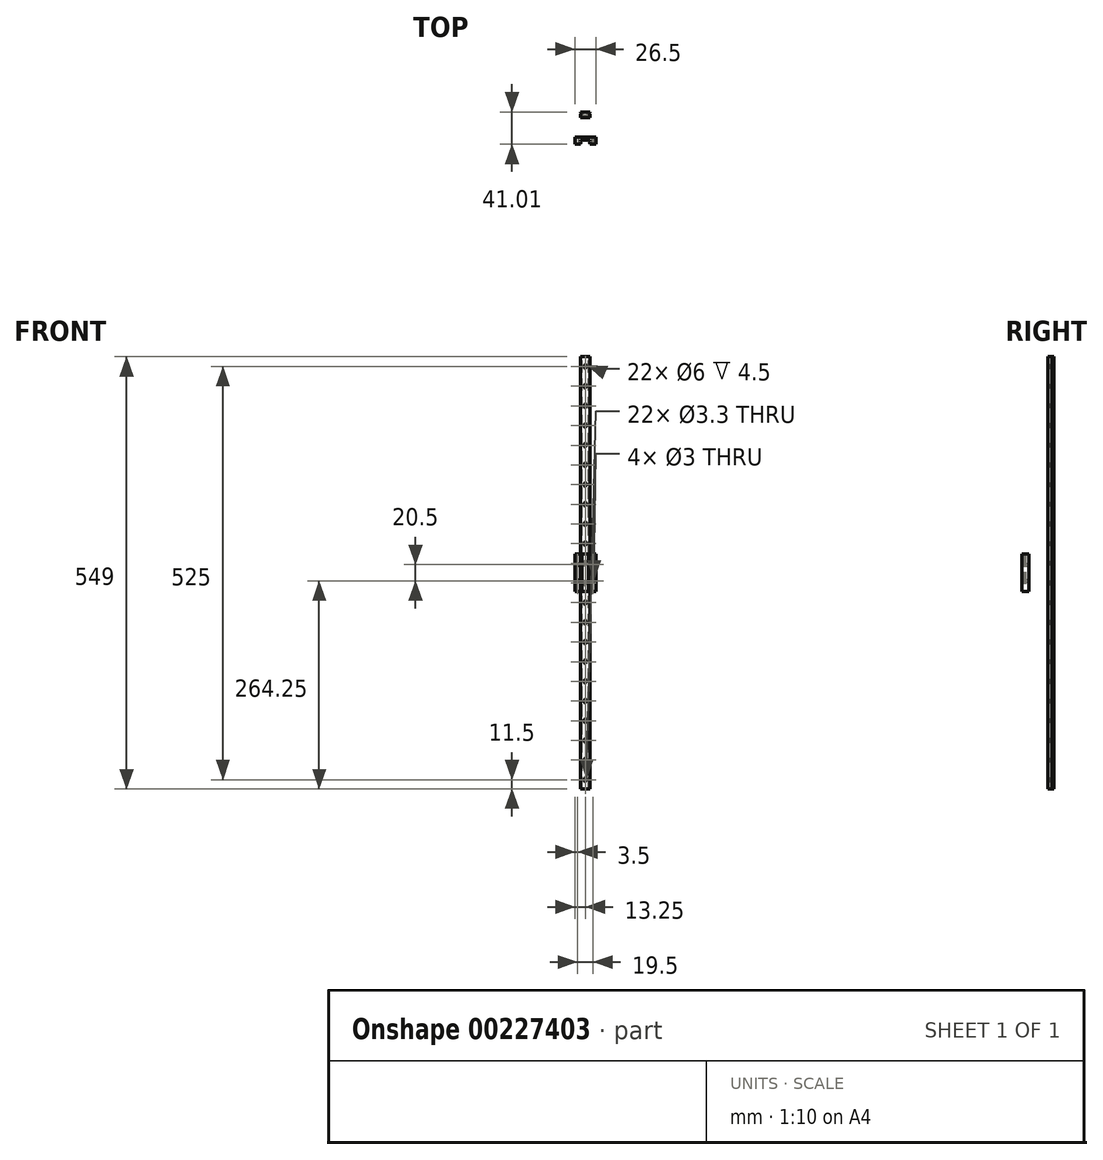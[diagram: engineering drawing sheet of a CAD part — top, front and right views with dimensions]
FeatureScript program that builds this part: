
annotation { "Feature Type Name" : "Feature", "Feature Type Description" : "" }
export const myFeature = defineFeature(function(context is Context, id is Id, definition is map)
    precondition{}
    {
        {
            var Q0;
            Q0=qCreatedBy(makeId("Front.planeOp"),FACE);
            var sketch = newSketch(context, id + "F0", { "sketchPlane" : qUnion([Q0])});
            skLineSegment(sketch, "E0.bottom", {"start": v(-6, 274.5) * mm, "end": v(6, 274.5) * mm});
            skLineSegment(sketch, "E0.top", {"start": v(-6, -274.5) * mm, "end": v(6, -274.5) * mm});
            skLineSegment(sketch, "E0.left", {"start": v(-6, 274.5) * mm, "end": v(-6, -274.5) * mm});
            skLineSegment(sketch, "E0.right", {"start": v(6, 274.5) * mm, "end": v(6, -274.5) * mm});
            skPoint(sketch, "E0.middle", {"position": v(0, 0) * mm});
            skSolve(sketch);
        }
        {
            var Q0;
            Q0 = qSketchRegion(id + "F0", true);
            extrude(context, id + "F1", {"entities" : qUnion([Q0]), "endBound" : BoundingType.SYMMETRIC, "depth" : 7.4 * mm});
        }
        {
            var Q0;
            Q0=makeQuery(id+"F1.opExtrude","SWEPT_FACE",FACE,{"disambiguationData":[OSD([sQuery(id+"F0.wireOp",EDGE,"E0.bottom")])]});
            var sketch = newSketch(context, id + "F2", { "sketchPlane" : qUnion([Q0])});
            skLineSegment(sketch, "E1", {"start": v(-6, 2.7) * mm, "end": v(-4, 1.7) * mm});
            skLineSegment(sketch, "E2", {"start": v(-4, 1.7) * mm, "end": v(-6, 1.03) * mm});
            skLineSegment(sketch, "E3.MirrorCS", {"start": v(6, 2.7) * mm, "end": v(4, 1.7) * mm});
            skLineSegment(sketch, "E4.MirrorCS", {"start": v(4, 1.7) * mm, "end": v(6, 1.03) * mm});
            skSolve(sketch);
        }
        {
            var Q0;
            {var subQ0=sQuery(id+"F2.wireOp",EDGE,"E1");Q0=makeQuery(id+"F2.imprint","IMPRINT",FACE,{"disambiguationData":[TD([[makeQuery(id+"F2.imprint","IMPRINT",EDGE,{"derivedFrom":subQ0}),-1.0]])]});}
            var Q1;
            {var subQ0=sQuery(id+"F2.wireOp",EDGE,"E3.MirrorCS");Q1=makeQuery(id+"F2.imprint","IMPRINT",FACE,{"disambiguationData":[TD([[makeQuery(id+"F2.imprint","IMPRINT",EDGE,{"derivedFrom":subQ0}),1.0]])]});}
            extrude(context, id + "F3", {"entities" : qUnion([Q0, Q1]), "operationType" : NewBodyOperationType.REMOVE, "endBound" : BoundingType.THROUGH_ALL, "oppositeDirection" : true, "depth" : 100 * mm});
        }
        {
            var Q0;
            Q0=makeQuery(id+"F1.opExtrude","CAP_FACE",FACE,{"disambiguationData":[OSD([sQuery(id+"F0.wireOp",EDGE,"E0.bottom"),sQuery(id+"F0.wireOp",EDGE,"E0.top"),sQuery(id+"F0.wireOp",EDGE,"E0.left"),sQuery(id+"F0.wireOp",EDGE,"E0.right")])],"isStart":true});
            var sketch = newSketch(context, id + "F4", { "sketchPlane" : qUnion([Q0])});
            skCircle(sketch, "E5", {"center": v(0, 262) * mm, "radius": 3 * mm});
            skPoint(sketch, "E6", {"position": v(0, 274.5) * mm});
            skCircle(sketch, "E7.0.1.0", {"center": v(0, 237) * mm, "radius": 3 * mm});
            skCircle(sketch, "E7.0.2.0", {"center": v(0, 212) * mm, "radius": 3 * mm});
            skCircle(sketch, "E7.0.3.0", {"center": v(0, 187) * mm, "radius": 3 * mm});
            skCircle(sketch, "E7.0.4.0", {"center": v(0, 162) * mm, "radius": 3 * mm});
            skCircle(sketch, "E7.0.5.0", {"center": v(0, 137) * mm, "radius": 3 * mm});
            skCircle(sketch, "E7.0.6.0", {"center": v(0, 112) * mm, "radius": 3 * mm});
            skCircle(sketch, "E7.0.7.0", {"center": v(0, 87) * mm, "radius": 3 * mm});
            skCircle(sketch, "E7.0.8.0", {"center": v(0, 62) * mm, "radius": 3 * mm});
            skCircle(sketch, "E7.0.9.0", {"center": v(0, 37) * mm, "radius": 3 * mm});
            skCircle(sketch, "E7.0.10.0", {"center": v(0, 12) * mm, "radius": 3 * mm});
            skCircle(sketch, "E7.0.11.0", {"center": v(0, -13) * mm, "radius": 3 * mm});
            skCircle(sketch, "E7.0.12.0", {"center": v(0, -38) * mm, "radius": 3 * mm});
            skCircle(sketch, "E7.0.13.0", {"center": v(0, -63) * mm, "radius": 3 * mm});
            skCircle(sketch, "E7.0.14.0", {"center": v(0, -88) * mm, "radius": 3 * mm});
            skCircle(sketch, "E7.0.15.0", {"center": v(0, -113) * mm, "radius": 3 * mm});
            skCircle(sketch, "E7.0.16.0", {"center": v(0, -138) * mm, "radius": 3 * mm});
            skCircle(sketch, "E7.0.17.0", {"center": v(0, -163) * mm, "radius": 3 * mm});
            skCircle(sketch, "E7.0.18.0", {"center": v(0, -188) * mm, "radius": 3 * mm});
            skCircle(sketch, "E7.0.19.0", {"center": v(0, -213) * mm, "radius": 3 * mm});
            skCircle(sketch, "E7.0.20.0", {"center": v(0, -238) * mm, "radius": 3 * mm});
            skCircle(sketch, "E7.0.21.0", {"center": v(0, -263) * mm, "radius": 3 * mm});
            skLineSegment(sketch, "E7.direction1", {"start": v(0, 262) * mm, "end": v(25, 262) * mm, "construction": true});
            skLineSegment(sketch, "E7.direction2", {"start": v(0, 262) * mm, "end": v(0, 237) * mm, "construction": true});
            skSolve(sketch);
        }
        {
            var Q0;
            Q0 = qSketchRegion(id + "F4", true);
            extrude(context, id + "F5", {"entities" : qUnion([Q0]), "operationType" : NewBodyOperationType.REMOVE, "oppositeDirection" : true, "depth" : 4.5 * mm});
        }
        {
            var Q0;
            Q0=makeQuery(id+"F1.opExtrude","CAP_FACE",FACE,{"disambiguationData":[OSD([sQuery(id+"F0.wireOp",EDGE,"E0.bottom"),sQuery(id+"F0.wireOp",EDGE,"E0.top"),sQuery(id+"F0.wireOp",EDGE,"E0.left"),sQuery(id+"F0.wireOp",EDGE,"E0.right")])],"isStart":false});
            var sketch = newSketch(context, id + "F6", { "sketchPlane" : qUnion([Q0])});
            skCircle(sketch, "E8", {"center": v(0, 262) * mm, "radius": 1.65 * mm});
            skCircle(sketch, "E9.0.1.0", {"center": v(0, 237) * mm, "radius": 1.65 * mm});
            skCircle(sketch, "E9.0.2.0", {"center": v(0, 212) * mm, "radius": 1.65 * mm});
            skCircle(sketch, "E9.0.3.0", {"center": v(0, 187) * mm, "radius": 1.65 * mm});
            skCircle(sketch, "E9.0.4.0", {"center": v(0, 162) * mm, "radius": 1.65 * mm});
            skCircle(sketch, "E9.0.5.0", {"center": v(0, 137) * mm, "radius": 1.65 * mm});
            skCircle(sketch, "E9.0.6.0", {"center": v(0, 112) * mm, "radius": 1.65 * mm});
            skCircle(sketch, "E9.0.7.0", {"center": v(0, 87) * mm, "radius": 1.65 * mm});
            skCircle(sketch, "E9.0.8.0", {"center": v(0, 62) * mm, "radius": 1.65 * mm});
            skCircle(sketch, "E9.0.9.0", {"center": v(0, 37) * mm, "radius": 1.65 * mm});
            skCircle(sketch, "E9.0.10.0", {"center": v(0, 12) * mm, "radius": 1.65 * mm});
            skCircle(sketch, "E9.0.11.0", {"center": v(0, -13) * mm, "radius": 1.65 * mm});
            skCircle(sketch, "E9.0.12.0", {"center": v(0, -38) * mm, "radius": 1.65 * mm});
            skCircle(sketch, "E9.0.13.0", {"center": v(0, -63) * mm, "radius": 1.65 * mm});
            skCircle(sketch, "E9.0.14.0", {"center": v(0, -88) * mm, "radius": 1.65 * mm});
            skCircle(sketch, "E9.0.15.0", {"center": v(0, -113) * mm, "radius": 1.65 * mm});
            skCircle(sketch, "E9.0.16.0", {"center": v(0, -138) * mm, "radius": 1.65 * mm});
            skCircle(sketch, "E9.0.17.0", {"center": v(0, -163) * mm, "radius": 1.65 * mm});
            skCircle(sketch, "E9.0.18.0", {"center": v(0, -188) * mm, "radius": 1.65 * mm});
            skCircle(sketch, "E9.0.19.0", {"center": v(0, -213) * mm, "radius": 1.65 * mm});
            skCircle(sketch, "E9.0.20.0", {"center": v(0, -238) * mm, "radius": 1.65 * mm});
            skCircle(sketch, "E9.0.21.0", {"center": v(0, -263) * mm, "radius": 1.65 * mm});
            skLineSegment(sketch, "E9.direction1", {"start": v(0, 262) * mm, "end": v(25, 262) * mm, "construction": true});
            skLineSegment(sketch, "E9.direction2", {"start": v(0, 262) * mm, "end": v(0, 237) * mm, "construction": true});
            skSolve(sketch);
        }
        {
            var Q0;
            Q0 = qSketchRegion(id + "F6", true);
            extrude(context, id + "F7", {"entities" : qUnion([Q0]), "operationType" : NewBodyOperationType.REMOVE, "oppositeDirection" : true, "depth" : 25 * mm});
        }
        {
            var Q0;
            Q0=qCreatedBy(makeId("Top.planeOp"),FACE);
            var sketch = newSketch(context, id + "F8", { "sketchPlane" : qUnion([Q0])});
            skLineSegment(sketch, "E10.bottom", {"start": v(-13.25, -28.3) * mm, "end": v(13.25, -28.3) * mm});
            skLineSegment(sketch, "E10.top", {"start": v(-13.25, -37.3) * mm, "end": v(-6, -37.3) * mm});
            skLineSegment(sketch, "E10.left", {"start": v(-13.25, -28.3) * mm, "end": v(-13.25, -37.3) * mm});
            skLineSegment(sketch, "E10.right", {"start": v(13.25, -28.3) * mm, "end": v(13.25, -37.3) * mm});
            skLineSegment(sketch, "E11.bottom", {"start": v(-6, -32.3) * mm, "end": v(6, -32.3) * mm});
            skLineSegment(sketch, "E12", {"start": v(-6, -33.3) * mm, "end": v(-4.16, -34.3) * mm});
            skLineSegment(sketch, "E13", {"start": v(-4.16, -34.3) * mm, "end": v(-6, -34.85) * mm});
            skLineSegment(sketch, "E14", {"start": v(-6, -32.3) * mm, "end": v(-6, -33.3) * mm});
            skLineSegment(sketch, "E15", {"start": v(-6, -34.85) * mm, "end": v(-6, -37.3) * mm});
            skLineSegment(sketch, "E16.MirrorCS", {"start": v(6, -33.3) * mm, "end": v(4.16, -34.3) * mm});
            skLineSegment(sketch, "E17.MirrorCS", {"start": v(4.16, -34.3) * mm, "end": v(6, -34.85) * mm});
            skLineSegment(sketch, "E18", {"start": v(6, -33.3) * mm, "end": v(6, -32.3) * mm});
            skLineSegment(sketch, "E19", {"start": v(6, -34.85) * mm, "end": v(6, -37.3) * mm});
            skLineSegment(sketch, "E20.trimOffspring", {"start": v(6, -37.3) * mm, "end": v(13.25, -37.3) * mm});
            skSolve(sketch);
        }
        {
            var Q0;
            Q0=makeQuery(id+"F8.imprint","IMPRINT",FACE,{"disambiguationData":[TD([[makeQuery(id+"F8.imprint","IMPRINT",EDGE,{"derivedFrom":sQuery(id+"F8.wireOp",EDGE,"E10.bottom")}),-1.0]])]});
            extrude(context, id + "F9", {"entities" : qUnion([Q0]), "endBound" : BoundingType.SYMMETRIC, "depth" : 47.5 * mm});
        }
        {
            var Q0;
            Q0=makeQuery(id+"F9.opExtrude","SWEPT_FACE",FACE,{"disambiguationData":[OSD([sQuery(id+"F8.wireOp",EDGE,"E10.bottom")])]});
            var sketch = newSketch(context, id + "F10", { "sketchPlane" : qUnion([Q0])});
            skCircle(sketch, "E21", {"center": v(9.75, -10.25) * mm, "radius": 1.5 * mm});
            skCircle(sketch, "E22.MirrorC", {"center": v(9.75, 10.25) * mm, "radius": 1.5 * mm});
            skCircle(sketch, "E23.MirrorC", {"center": v(-9.75, 10.25) * mm, "radius": 1.5 * mm});
            skCircle(sketch, "E24.MirrorC", {"center": v(-9.75, -10.25) * mm, "radius": 1.5 * mm});
            skSolve(sketch);
        }
        {
            var Q0;
            Q0 = qSketchRegion(id + "F10", true);
            extrude(context, id + "F11", {"entities" : qUnion([Q0]), "operationType" : NewBodyOperationType.REMOVE, "oppositeDirection" : true, "depth" : 25 * mm});
        }
    });
